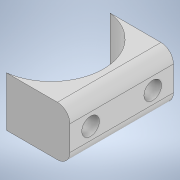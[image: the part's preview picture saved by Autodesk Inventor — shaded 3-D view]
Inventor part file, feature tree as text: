
AUTODESK INVENTOR PART (.ipt)
format: ipt  version: 2020 (Build 240168000, 168)  size: 126,464 bytes
history: native  units: in
note: dims shown in document units (in); Inventor stores cm internally (conversion verified against a paired STEP export)
features: sketch x2, extrude x1, hole x1, fillet x1
ambient origin geometry x8: Origin, YZ Plane, XZ Plane, XY Plane, X Axis, Y Axis, Z Axis, Center Point
bodies: Solid1 (feature_tree)
feature tree (5):
  extrude  "Extrusion1"  Depth=1.04in
  hole  "Hole1"  [1 undecoded]
  fillet  "Fillet1"  Radius=1.05in
  sketch  "Sketch1"  dims[d0=1.04in d1=1.04in]
  sketch  "Sketch2"  dims[d2=0.708in d3=0.0in d4=1.05in d5=0.5in d6=0.0in d7=0.25in d8=90.0deg d9=0.312in d10=0.0in d11=0.312in d12=180.0deg d13=0.177in d14=0.75in d15=0.332in d16=0.25in d17=0.5635in d18=1.378in d19=0.0in d20=0.125in]
note: 1 required parameter value undecoded (feature->parameter linkage not recoverable at this tier; creation-order binding heuristic only, values carry confidence <= 0.55)
